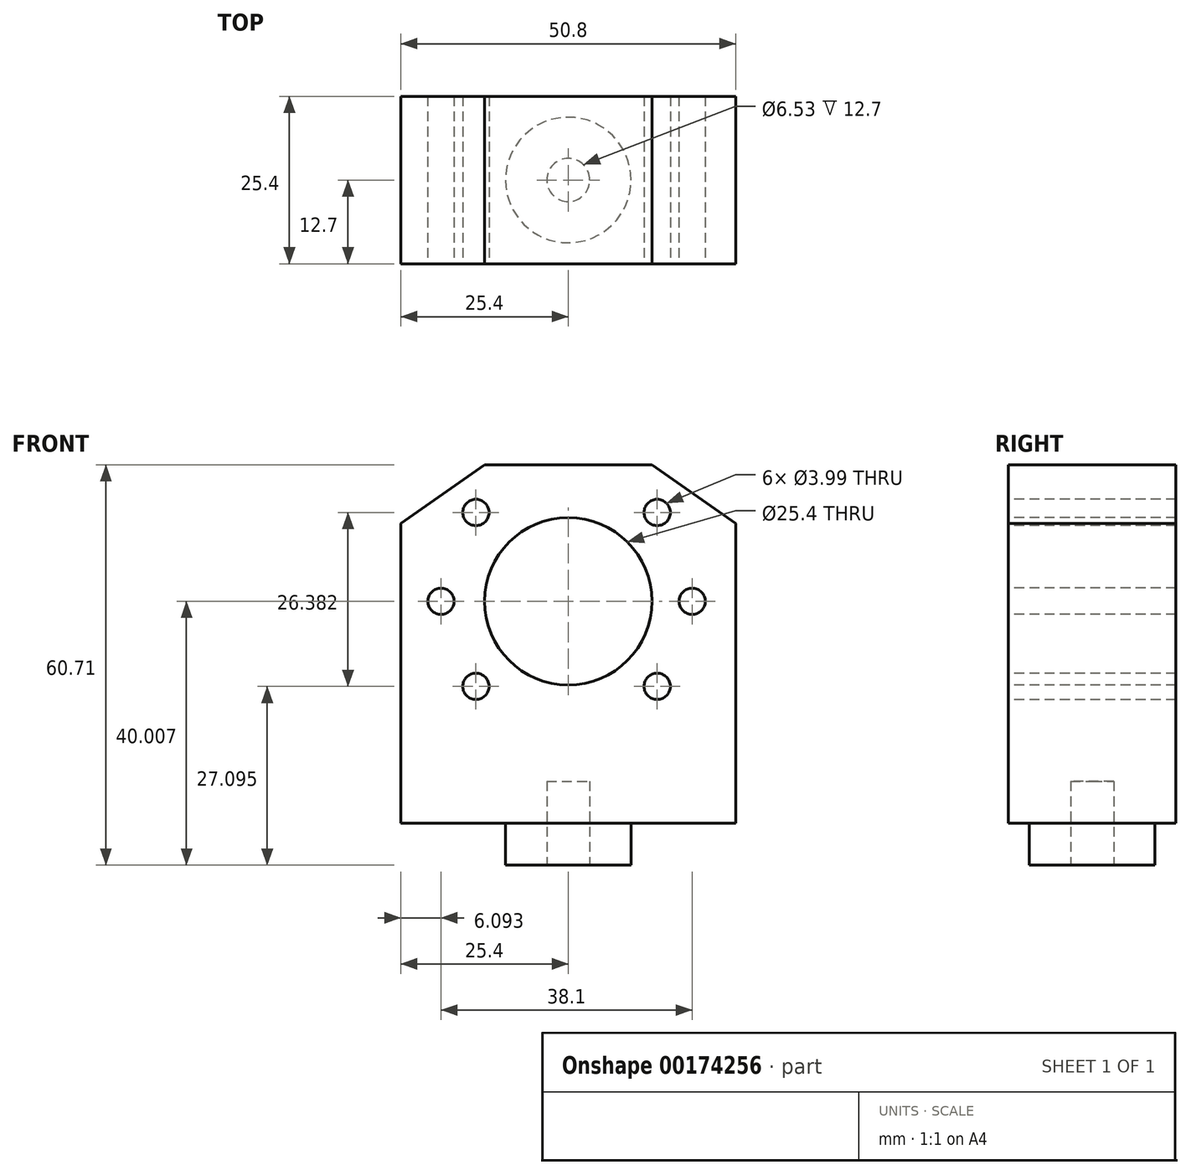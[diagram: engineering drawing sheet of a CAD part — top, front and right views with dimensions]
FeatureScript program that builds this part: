
annotation { "Feature Type Name" : "Feature", "Feature Type Description" : "" }
export const myFeature = defineFeature(function(context is Context, id is Id, definition is map)
    precondition{}
    {
        {
            var Q0;
            Q0=qCreatedBy(makeId("Top.planeOp"),FACE);
            var sketch = newSketch(context, id + "F0", { "sketchPlane" : qUnion([Q0])});
            skLineSegment(sketch, "E0.bottom", {"start": v(-25.4, -12.7) * mm, "end": v(25.4, -12.7) * mm});
            skLineSegment(sketch, "E0.top", {"start": v(-25.4, 12.7) * mm, "end": v(25.4, 12.7) * mm});
            skLineSegment(sketch, "E0.left", {"start": v(-25.4, -12.7) * mm, "end": v(-25.4, 12.7) * mm});
            skLineSegment(sketch, "E0.right", {"start": v(25.4, -12.7) * mm, "end": v(25.4, 12.7) * mm});
            skPoint(sketch, "E0.middle", {"position": v(0, 0) * mm});
            skSolve(sketch);
        }
        {
            var Q0;
            Q0=qSketchRegion(id+"F0",true);
            extrude(context, id + "F1", {"entities" : qUnion([Q0]), "endBound" : BoundingType.SYMMETRIC, "oppositeDirection" : true, "depth" : 54.36 * mm});
        }
        {
            var Q0;
            Q0=makeQuery(id+"F1.opExtrude","CAP_EDGE",EDGE,{"disambiguationData":[OSD([sQuery(id+"F0.wireOp",EDGE,"E0.left")])],"isStart":true});
            var Q1;
            Q1=makeQuery(id+"F1.opExtrude","CAP_EDGE",EDGE,{"disambiguationData":[OSD([sQuery(id+"F0.wireOp",EDGE,"E0.right")])],"isStart":true});
            chamfer(context, id + "F2", {"entities" : qUnion([Q0, Q1]), "chamferType" : ChamferType.TWO_OFFSETS, "width1" : 8.9 * mm, "oppositeDirection" : false, "width2" : 12.7 * mm, "tangentPropagation" : true});
        }
        {
            var Q0;
            Q0=makeQuery(id+"F0erdF5z4OaUTfu_1.boolean.opBoolean","MERGE",FACE,{"derivedFrom":[makeQuery(id+"F1.opExtrude","SWEPT_FACE",FACE,{"disambiguationData":[OSD([sQuery(id+"F0.wireOp",EDGE,"E0.bottom")])]}),makeQuery(id+"F0erdF5z4OaUTfu_1.opExtrude","SWEPT_FACE",FACE,{"disambiguationData":[OSD([sQuery(id+"FmbxTDfUtuEb3ht_1.wireOp",EDGE,"BPEYb6zV-gMC1-sygU-iM1X-TKquUu5BGLO9.top")])]})]});
            var sketch = newSketch(context, id + "F3", { "sketchPlane" : qUnion([Q0])});
            skCircle(sketch, "E1", {"center": v(0, 6.48) * mm, "radius": 12.7 * mm});
            skSolve(sketch);
        }
        {
            var Q0;
            Q0=makeQuery(id+"F3.imprint","IMPRINT",FACE,{"disambiguationData":[TD([[makeQuery(id+"F3.imprint","IMPRINT",EDGE,{"derivedFrom":sQuery(id+"F3.wireOp",EDGE,"E1")}),-1.0]])]});
            var sketch = newSketch(context, id + "F4", { "sketchPlane" : qUnion([Q0])});
            skCircle(sketch, "E2", {"center": v(-14, 19.95) * mm, "radius": 2 * mm});
            skCircle(sketch, "E3", {"center": v(13.49, 19.95) * mm, "radius": 2 * mm});
            skCircle(sketch, "E4", {"center": v(18.8, 6.48) * mm, "radius": 2 * mm});
            skCircle(sketch, "E5", {"center": v(13.49, -6.43) * mm, "radius": 2 * mm});
            skCircle(sketch, "E6", {"center": v(-14, -6.43) * mm, "radius": 2 * mm});
            skCircle(sketch, "E7", {"center": v(-19.3, 6.48) * mm, "radius": 2 * mm});
            skSolve(sketch);
        }
        {
            var Q0;
            Q0=qSketchRegion(id+"F4",true);
            extrude(context, id + "F5", {"entities" : qUnion([Q0]), "operationType" : NewBodyOperationType.REMOVE, "endBound" : BoundingType.THROUGH_ALL, "oppositeDirection" : true, "depth" : 25.4 * mm});
        }
        {
            var Q0;
            Q0=makeQuery(id+"F3.imprint","IMPRINT",FACE,{"disambiguationData":[TD([[makeQuery(id+"F3.imprint","IMPRINT",EDGE,{"derivedFrom":sQuery(id+"F3.wireOp",EDGE,"E1")}),1.0]])]});
            var Q1;
            Q1=sQuery(id+"F3.wireOp",EDGE,"E1");
            extrude(context, id + "F6", {"entities" : qUnion([Q0]), "operationType" : NewBodyOperationType.REMOVE, "surfaceEntities" : qUnion([Q1]), "endBound" : BoundingType.THROUGH_ALL, "oppositeDirection" : true, "depth" : 25.4 * mm});
        }
        {
            var Q0;
            Q0=makeQuery(id+"F1.opExtrude","CAP_FACE",FACE,{"disambiguationData":[OSD([sQuery(id+"F0.wireOp",EDGE,"E0.bottom"),sQuery(id+"F0.wireOp",EDGE,"E0.top"),sQuery(id+"F0.wireOp",EDGE,"E0.left"),sQuery(id+"F0.wireOp",EDGE,"E0.right")])],"isStart":false});
            var sketch = newSketch(context, id + "F7", { "sketchPlane" : qUnion([Q0])});
            skCircle(sketch, "E8", {"center": v(0, 0) * mm, "radius": 9.52 * mm});
            skSolve(sketch);
        }
        {
            var Q0;
            Q0 = qSketchRegion(id + "F7", true);
            extrude(context, id + "F8", {"entities" : qUnion([Q0]), "operationType" : NewBodyOperationType.ADD, "depth" : 6.35 * mm});
        }
        {
            var Q0;
            Q0=makeQuery(id+"F8.opExtrude","CAP_FACE",FACE,{"disambiguationData":[OSD([sQuery(id+"F7.wireOp",EDGE,"E8")])],"isStart":false});
            var sketch = newSketch(context, id + "F9", { "sketchPlane" : qUnion([Q0])});
            skCircle(sketch, "E9", {"center": v(0, 0) * mm, "radius": 3.26 * mm});
            skSolve(sketch);
        }
        {
            var Q0;
            Q0 = qSketchRegion(id + "F9", true);
            extrude(context, id + "F10", {"entities" : qUnion([Q0]), "operationType" : NewBodyOperationType.REMOVE, "oppositeDirection" : true, "depth" : 12.7 * mm});
        }
    });
